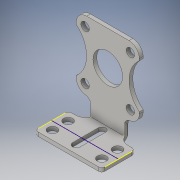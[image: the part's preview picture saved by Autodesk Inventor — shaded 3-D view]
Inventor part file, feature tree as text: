
AUTODESK INVENTOR PART (.ipt)
format: ipt  version: 2016 (Build 200138000, 138)  size: 249,344 bytes
history: native  units: in
note: dims shown in document units (in); Inventor stores cm internally (conversion verified against a paired STEP export)
features: sketch x10, extrude x6, fillet x3
ambient origin geometry x8: Origin, YZ Plane, XZ Plane, XY Plane, X Axis, Y Axis, Z Axis, Center Point
bodies: Solid1 (feature_tree)
feature tree (19):
  extrude  "Extrusion1"  Depth=0.82in
  extrude  "Extrusion3"  Depth=0.135in
  sketch  "Sketch4"  dims[d10=0.11in d18=0.083in d20=0.377in]
  sketch  "Sketch5"  dims[d21=0.05in d22=0.0in d28=0.212in]
  sketch  "Sketch6"  dims[d29=0.104in d30=0.05in d31=0.0in d34=0.05in d35=0.0in d36=0.05in]
  extrude  "Extrusion5"  Depth=0.083in
  fillet  "Fillet1"  Radius=0.377in
  extrude  "Extrusion8"  Depth=0.05in
  extrude  "Extrusion9"  Depth=0.05in TaperAngle=0.0deg
  fillet  "Fillet2"  Radius=0.05in
  sketch  "Sketch11"  dims[d62=0.433in]
  fillet  "Fillet3"  Radius=0.05in
  sketch  "Sketch13"  dims[d63=0.05in d64=0.0in]
  extrude  "Extrusion10"  Depth=0.05in TaperAngle=0.0deg
  sketch  "Sketch14"  dims[d65=0.125in d66=0.04in d69=0.119in d74=0.104in d75=0.077in d76=0.098in d77=0.05in d78=0.0in d79=0.085in d80=0.524in d81=0.1145in d82=0.1125in]
  sketch  "Sketch1"  dims[d0=0.896in d1=0.82in]
  sketch  "Sketch3"  dims[d2=0.386in d9=0.135in]
  sketch  "Sketch7"  dims[d57=0.08in d58=0.05in d59=0.0in]
  sketch  "Sketch10"  dims[d61=0.868in]
